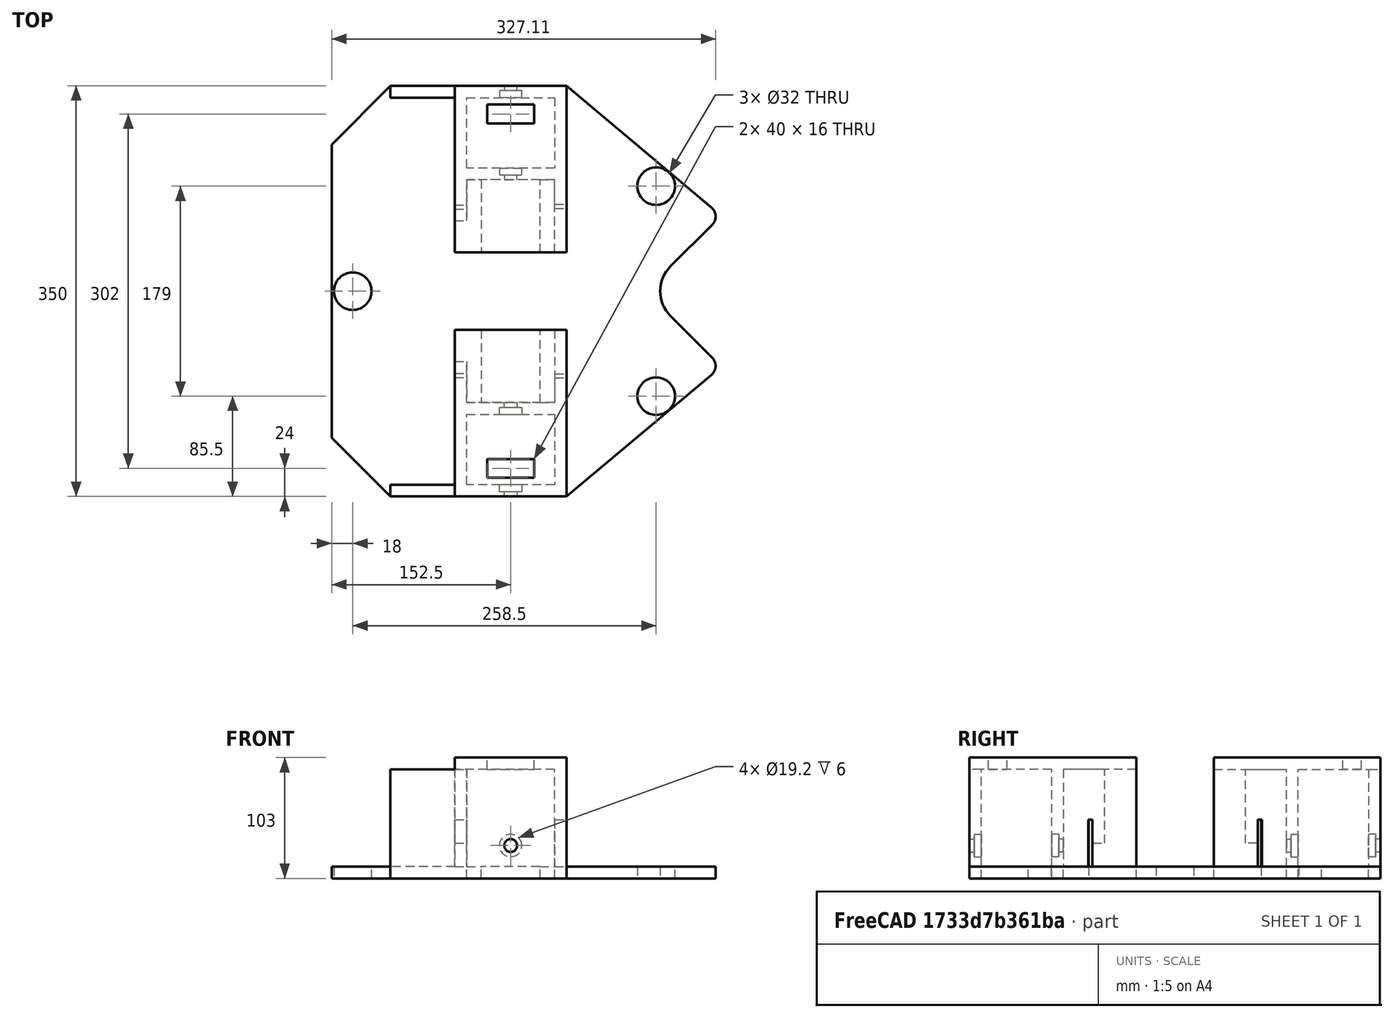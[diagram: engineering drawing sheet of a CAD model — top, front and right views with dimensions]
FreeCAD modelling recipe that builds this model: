
FCSTD DOCUMENT  (FreeCAD 0.15R4669 (Git))
Label: BR_assemblageBaseRoulante
License: CC-BY 3.0
LicenseURL: http://creativecommons.org/licenses/by/3.0/
objects: Part::Feature×6, Part::MultiFuse×2, Part::Mirroring×1
note: 9 computed .brp shape members not serialized (recipe doc carries the construction recipe); baked Part::Feature solids carry a one-line shape summary decoded from their .brp

FEATURE [Part::Feature] Extrude004  label="supportMoteurTop"
  Placement = pos=(0,175,65) rot=(0,0,1;0rad)
  shape: bbox 95 x 142 x 10 mm, 10 faces (baked)
FEATURE [Part::Feature] Extrude005  label="supportMoteurS"
  Placement = pos=(-47.5,165,0) rot=(0,0,1;0rad)
  shape: bbox 10 x 105 x 83 mm, 10 faces (baked)
FEATURE [Part::Feature] Cut001  label="supportMoteurE"
  Placement = pos=(0,105,0) rot=(0,0,1;3.14159rad)
  shape: bbox 75 x 10 x 83 mm, 9 faces (baked)
FEATURE [Part::Feature] Extrude002  label="supportMoteurN"
  Placement = pos=(37.5,165,0) rot=(0,0,1;0rad)
  shape: bbox 10 x 132 x 83 mm, 10 faces (baked)
FEATURE [Part::Feature] Cut  label="supportMoteurW"
  Placement = pos=(0,165,0) rot=(0,0,1;0rad)
  shape: bbox 150 x 10 x 83 mm, 9 faces (baked)
FEATURE [Part::MultiFuse] Fusion  label="supportMoteur"
  Shapes = -> [Extrude004,Extrude005,Cut001,Extrude002,Cut]
FEATURE [Part::Mirroring] Part__Mirroring  label="supportMoteur (Mirror #1)"
  Base = (0,0,0)
  Normal = (0,1,0)
  Source = -> Fusion
FEATURE [Part::Feature] Extrude  label="plaqueChassis"
  Placement = pos=(0,0,-28) rot=(0,0,1;0rad)
  shape: bbox 327.1 x 350 x 10 mm, 33 faces (baked)
FEATURE [Part::MultiFuse] Fusion001  label="baseRoulante"
  Shapes = -> [Part__Mirroring,Fusion,Extrude]
